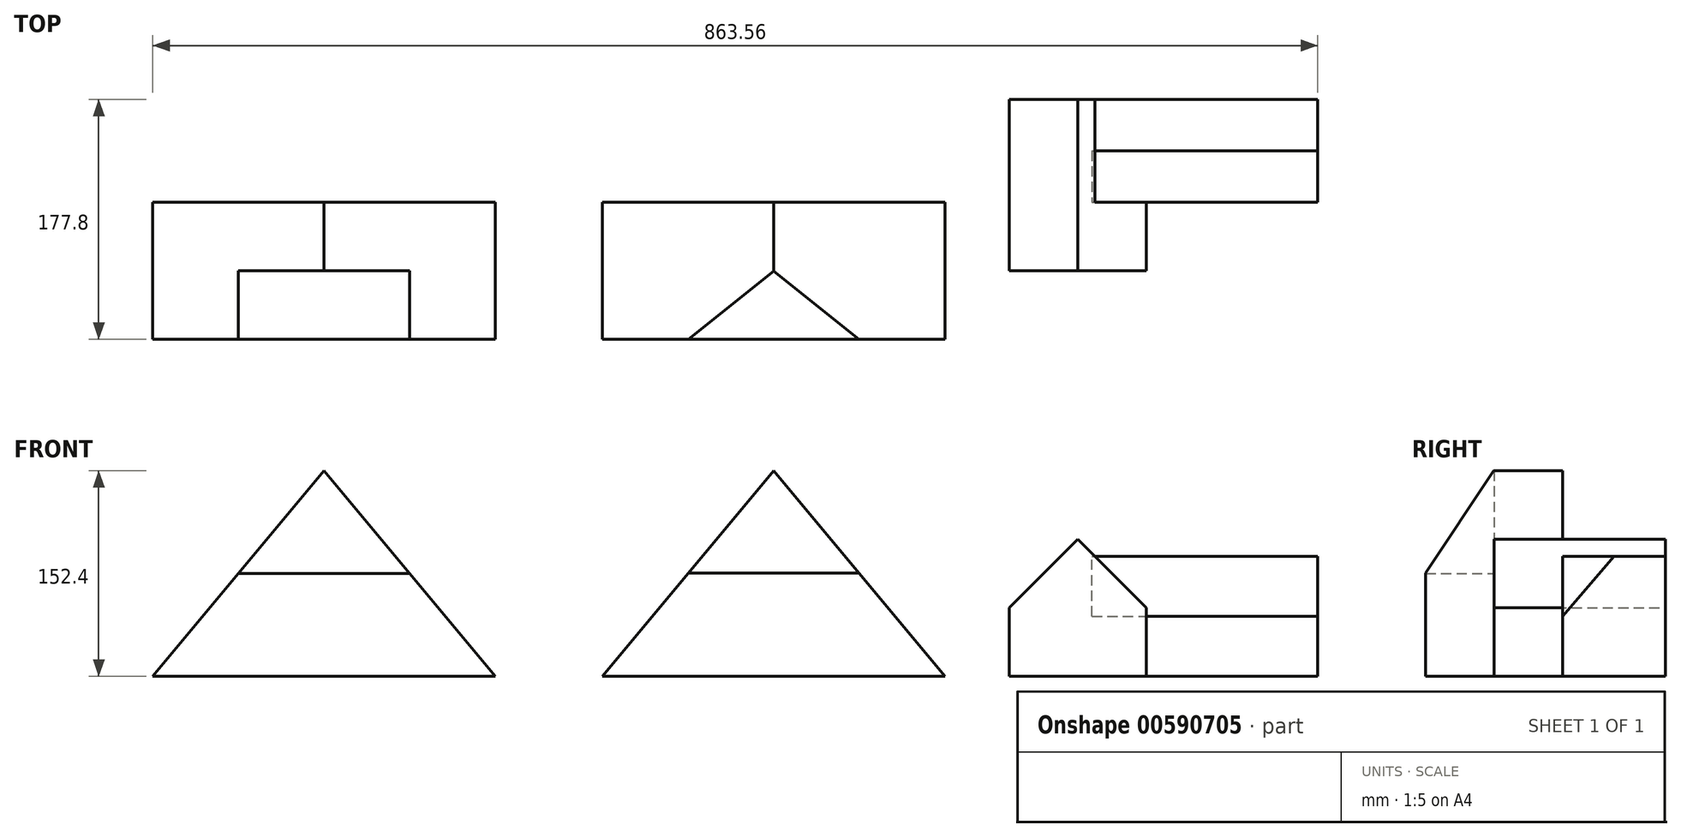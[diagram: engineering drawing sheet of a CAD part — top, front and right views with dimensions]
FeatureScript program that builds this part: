
annotation { "Feature Type Name" : "Feature", "Feature Type Description" : "" }
export const myFeature = defineFeature(function(context is Context, id is Id, definition is map)
    precondition{}
    {
        {
            var Q0;
            Q0=qCreatedBy(makeId("Front.planeOp"),FACE);
            var sketch = newSketch(context, id + "F0", { "sketchPlane" : qUnion([Q0])});
            skLineSegment(sketch, "E0", {"start": v(0, 0) * mm, "end": v(-254, 0) * mm});
            skLineSegment(sketch, "E1", {"start": v(-254, 0) * mm, "end": v(-127, 0) * mm});
            skLineSegment(sketch, "E2", {"start": v(-127, 0) * mm, "end": v(-127, 152.4) * mm});
            skLineSegment(sketch, "E3", {"start": v(-127, 152.4) * mm, "end": v(-254, 0) * mm});
            skLineSegment(sketch, "E4", {"start": v(-127, 152.4) * mm, "end": v(0, 0) * mm});
            skSolve(sketch);
        }
        {
            var Q0;
            Q0=makeQuery(id+"F0.imprint","IMPRINT",FACE,{"disambiguationData":[TD([[makeQuery(id+"F0.imprint","IMPRINT",EDGE,{"derivedFrom":sQuery(id+"F0.wireOp",EDGE,"E0")}),-1.0]])]});
            var Q1;
            Q1=makeQuery(id+"F0.imprint","IMPRINT",FACE,{"disambiguationData":[TD([[makeQuery(id+"F0.imprint","IMPRINT",EDGE,{"derivedFrom":sQuery(id+"F0.wireOp",EDGE,"E1")}),1.0]])]});
            extrude(context, id + "F1", {"entities" : qUnion([Q0, Q1]), "depth" : 50.8 * mm, "offsetDistance" : 25.4 * mm});
        }
        {
            var Q0;
            Q0=makeQuery(id+"F1.opExtrude","CAP_FACE",FACE,{"disambiguationData":[OSD([sQuery(id+"F0.wireOp",EDGE,"E0"),sQuery(id+"F0.wireOp",EDGE,"E1"),sQuery(id+"F0.wireOp",EDGE,"E3"),sQuery(id+"F0.wireOp",EDGE,"E4")])],"isStart":false});
            var sketch = newSketch(context, id + "F2", { "sketchPlane" : qUnion([Q0])});
            skLineSegment(sketch, "E5", {"start": v(-254, 0) * mm, "end": v(-127, 0) * mm});
            skLineSegment(sketch, "E6", {"start": v(-127, 0) * mm, "end": v(-127, 76.2) * mm});
            skLineSegment(sketch, "E7", {"start": v(-127, 76.2) * mm, "end": v(-190.5, 76.2) * mm});
            skLineSegment(sketch, "E8", {"start": v(-190.5, 76.2) * mm, "end": v(-63.5, 76.2) * mm});
            skSolve(sketch);
        }
        {
            var Q0;
            Q0 = qSketchRegion(id + "F2", true);
            var Q1;
            {var subQ0=sQuery(id+"F2.wireOp",EDGE,"E5");Q1=makeQuery(id+"F2.imprint","IMPRINT",FACE,{"disambiguationData":[TD([[makeQuery(id+"F2.imprint","IMPRINT",EDGE,{"derivedFrom":subQ0}),-1.0]])]});}
            var Q2;
            {var subQ0=sQuery(id+"F2.wireOp",EDGE,"E6");Q2=makeQuery(id+"F2.imprint","IMPRINT",FACE,{"disambiguationData":[TD([[makeQuery(id+"F2.imprint","IMPRINT",EDGE,{"derivedFrom":subQ0}),-1.0]])]});}
            extrude(context, id + "F3", {"entities" : qUnion([Q0, Q1, Q2]), "operationType" : NewBodyOperationType.ADD, "depth" : 50.8 * mm, "offsetDistance" : 25.4 * mm});
        }
        {
            var Q0;
            Q0=qCreatedBy(makeId("Front.planeOp"),FACE);
            var sketch = newSketch(context, id + "F4", { "sketchPlane" : qUnion([Q0])});
            skLineSegment(sketch, "E9", {"start": v(79.4, 0) * mm, "end": v(333.4, 0) * mm});
            skLineSegment(sketch, "E10", {"start": v(79.4, 0) * mm, "end": v(206.4, 0) * mm});
            skLineSegment(sketch, "E11", {"start": v(206.4, 0) * mm, "end": v(206.4, 152.4) * mm});
            skLineSegment(sketch, "E12", {"start": v(206.4, 152.4) * mm, "end": v(79.4, 0) * mm});
            skLineSegment(sketch, "E13", {"start": v(206.4, 152.4) * mm, "end": v(333.4, 0) * mm});
            skSolve(sketch);
        }
        {
            var Q0;
            Q0 = qSketchRegion(id + "F4", true);
            var Q1;
            Q1=makeQuery(id+"F4.imprint","IMPRINT",FACE,{"disambiguationData":[TD([[makeQuery(id+"F4.imprint","IMPRINT",EDGE,{"derivedFrom":sQuery(id+"F4.wireOp",EDGE,"E10")}),1.0]])]});
            var Q2;
            Q2 = qSketchRegion(id + "F2", true);
            extrude(context, id + "F5", {"entities" : qUnion([Q0, Q1, Q2]), "depth" : 101.6 * mm, "offsetDistance" : 25.4 * mm});
        }
        {
            var Q0;
            Q0=qCreatedBy(makeId("Right.planeOp"),FACE);
            cPlane(context, id + "F6", {"entities" : qUnion([Q0]), "cplaneType" : CPlaneType.OFFSET, "offset" : 342.14 * mm, "width" : 152.4 * mm, "height" : 152.4 * mm});
        }
        {
            var Q0;
            Q0=qCreatedBy(id+"F6.planeOp",FACE);
            var sketch = newSketch(context, id + "F7", { "sketchPlane" : qUnion([Q0])});
            skLineSegment(sketch, "E14", {"start": v(-101.84, 152.4) * mm, "end": v(-51.04, 152.4) * mm});
            skLineSegment(sketch, "E15", {"start": v(-51.04, 152.4) * mm, "end": v(-101.84, 76.2) * mm});
            skLineSegment(sketch, "E16", {"start": v(-101.84, 76.2) * mm, "end": v(-101.84, 152.4) * mm});
            skSolve(sketch);
        }
        {
            var Q0;
            Q0=makeQuery(id+"F7.imprint","IMPRINT",FACE,{"disambiguationData":[TD([[makeQuery(id+"F7.imprint","IMPRINT",EDGE,{"derivedFrom":sQuery(id+"F7.wireOp",EDGE,"E14")}),-1.0]])]});
            extrude(context, id + "F8", {"entities" : qUnion([Q0]), "operationType" : NewBodyOperationType.REMOVE, "oppositeDirection" : true, "depth" : 239.52 * mm, "offsetDistance" : 25.4 * mm});
        }
        {
            var Q0;
            Q0=qCreatedBy(makeId("Front.planeOp"),FACE);
            var sketch = newSketch(context, id + "F9", { "sketchPlane" : qUnion([Q0])});
            skLineSegment(sketch, "E17", {"start": v(380.96, 0) * mm, "end": v(431.76, 0) * mm});
            skLineSegment(sketch, "E18", {"start": v(380.96, 0) * mm, "end": v(380.96, 50.8) * mm});
            skLineSegment(sketch, "E19", {"start": v(431.76, 0) * mm, "end": v(482.56, 0) * mm});
            skLineSegment(sketch, "E20", {"start": v(482.56, 0) * mm, "end": v(482.56, 50.8) * mm});
            skLineSegment(sketch, "E21", {"start": v(380.96, 50.8) * mm, "end": v(431.76, 101.6) * mm});
            skLineSegment(sketch, "E22", {"start": v(482.56, 50.8) * mm, "end": v(431.76, 101.6) * mm});
            skLineSegment(sketch, "E23", {"start": v(482.56, 0) * mm, "end": v(609.56, 0) * mm});
            skLineSegment(sketch, "E24", {"start": v(609.56, 0) * mm, "end": v(609.56, 50.8) * mm});
            skLineSegment(sketch, "E25", {"start": v(609.56, 50.8) * mm, "end": v(609.56, 88.9) * mm});
            skLineSegment(sketch, "E26", {"start": v(609.56, 88.9) * mm, "end": v(444.46, 88.9) * mm});
            skLineSegment(sketch, "E27", {"start": v(380.96, 0) * mm, "end": v(482.56, 0) * mm});
            skLineSegment(sketch, "E28", {"start": v(482.56, 50.8) * mm, "end": v(609.56, 50.8) * mm});
            skSolve(sketch);
        }
        {
            var Q0;
            Q0=makeQuery(id+"F9.imprint","IMPRINT",FACE,{"disambiguationData":[TD([[makeQuery(id+"F9.imprint","IMPRINT",EDGE,{"derivedFrom":sQuery(id+"F9.wireOp",EDGE,"E18")}),-1.0]])]});
            extrude(context, id + "F10", {"entities" : qUnion([Q0]), "depth" : 50.8 * mm, "offsetDistance" : 25.4 * mm, "hasSecondDirection" : true, "secondDirectionOppositeDirection" : true, "secondDirectionDepth" : 76.2 * mm});
        }
        {
            var Q0;
            {var subQ1=sQuery(id+"F9.wireOp",EDGE,"E20");Q0=makeQuery(id+"F9.imprint","IMPRINT",FACE,{"disambiguationData":[TD([[makeQuery(id+"F9.imprint","IMPRINT",EDGE,{"derivedFrom":subQ1}),-1.0]])]});}
            extrude(context, id + "F11", {"entities" : qUnion([Q0]), "oppositeDirection" : true, "depth" : 76.2 * mm, "offsetDistance" : 25.4 * mm});
        }
        {
            var Q0;
            Q0=makeQuery(id+"F9.imprint","IMPRINT",FACE,{"disambiguationData":[TD([[makeQuery(id+"F9.imprint","IMPRINT",EDGE,{"derivedFrom":sQuery(id+"F9.wireOp",EDGE,"E25")}),1.0]])]});
            extrude(context, id + "F12", {"entities" : qUnion([Q0]), "operationType" : NewBodyOperationType.ADD, "oppositeDirection" : true, "depth" : 76.2 * mm, "offsetDistance" : 25.4 * mm});
        }
        {
            var Q0;
            Q0=makeQuery(id+"F12.boolean.opBoolean","MERGE",FACE,{"derivedFrom":[makeQuery(id+"F11.opExtrude","SWEPT_FACE",FACE,{"disambiguationData":[OSD([sQuery(id+"F9.wireOp",EDGE,"E24")])]}),makeQuery(id+"F12.opExtrude","SWEPT_FACE",FACE,{"disambiguationData":[OSD([sQuery(id+"F9.wireOp",EDGE,"E25")])]})]});
            var sketch = newSketch(context, id + "F13", { "sketchPlane" : qUnion([Q0])});
            skLineSegment(sketch, "E29", {"start": v(0, 0) * mm, "end": v(0, 44.45) * mm});
            skLineSegment(sketch, "E30", {"start": v(0, 44.45) * mm, "end": v(38.1, 88.9) * mm});
            skLineSegment(sketch, "E31", {"start": v(38.1, 88.9) * mm, "end": v(76.2, 44.45) * mm});
            skLineSegment(sketch, "E32", {"start": v(76.2, 44.45) * mm, "end": v(76.2, 0) * mm});
            skLineSegment(sketch, "E33", {"start": v(76.2, 0) * mm, "end": v(0, 0) * mm});
            skLineSegment(sketch, "E34", {"start": v(0, 44.45) * mm, "end": v(0, 88.9) * mm});
            skLineSegment(sketch, "E35", {"start": v(0, 88.9) * mm, "end": v(38.1, 88.9) * mm});
            skLineSegment(sketch, "E36", {"start": v(38.1, 88.9) * mm, "end": v(76.2, 88.9) * mm});
            skLineSegment(sketch, "E37", {"start": v(76.2, 88.9) * mm, "end": v(76.2, 44.45) * mm});
            skSolve(sketch);
        }
        {
            var Q0;
            Q0=makeQuery(id+"F13.imprint","IMPRINT",FACE,{"disambiguationData":[TD([[makeQuery(id+"F13.imprint","IMPRINT",EDGE,{"derivedFrom":sQuery(id+"F13.wireOp",EDGE,"E30")}),1.0]])]});
            extrude(context, id + "F14", {"entities" : qUnion([Q0]), "operationType" : NewBodyOperationType.REMOVE, "oppositeDirection" : true, "depth" : 167.39 * mm, "offsetDistance" : 25.4 * mm});
        }
    });
